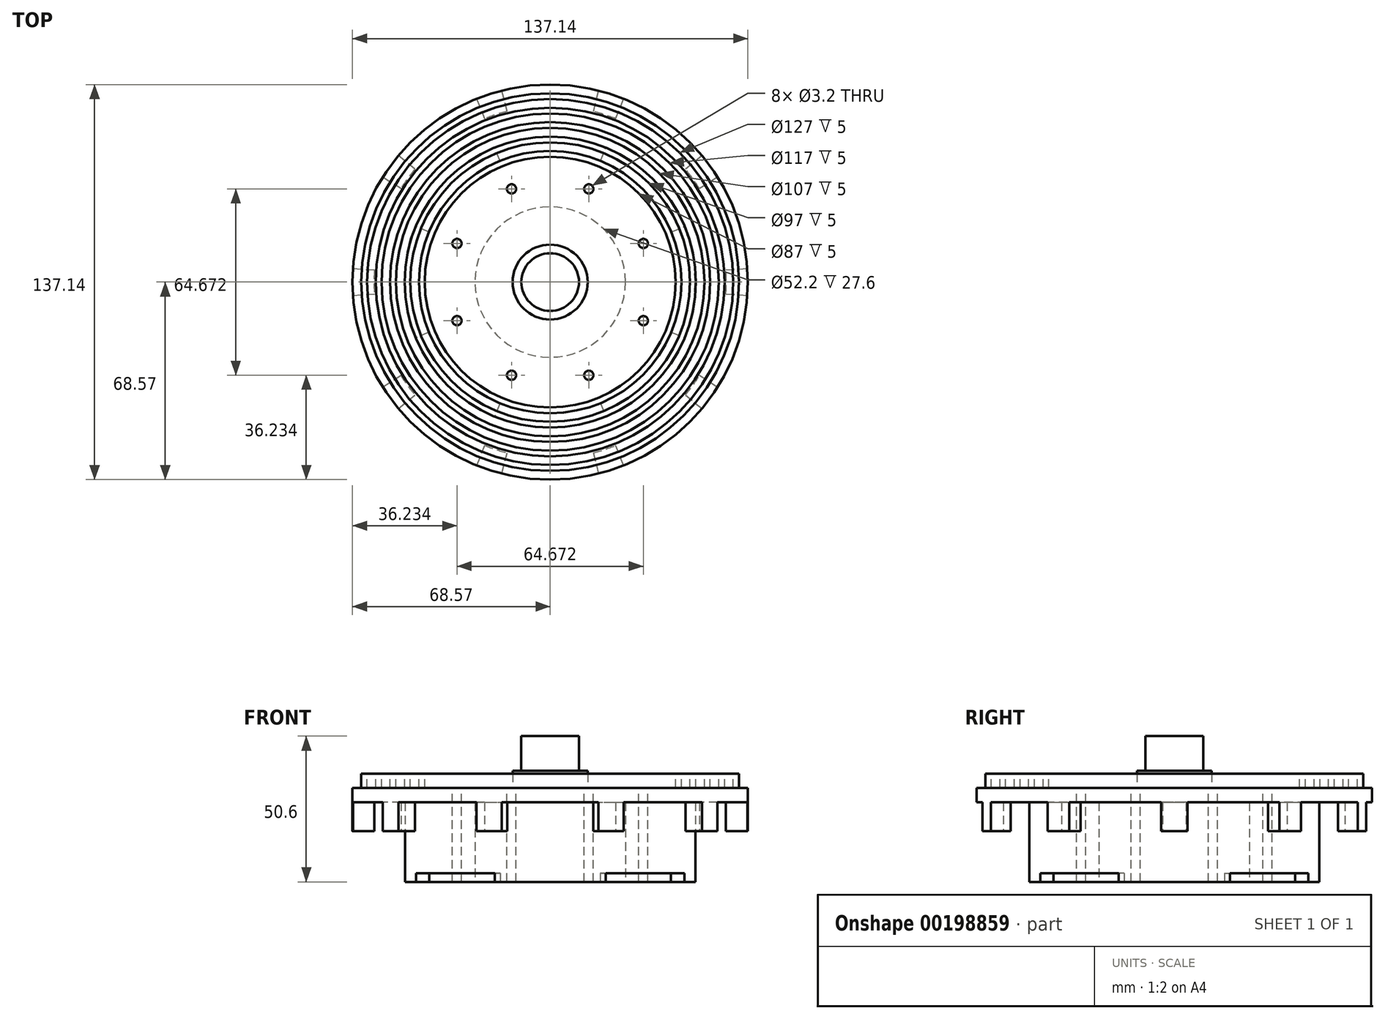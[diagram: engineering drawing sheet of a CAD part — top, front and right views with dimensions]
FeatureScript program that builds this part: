
annotation { "Feature Type Name" : "Feature", "Feature Type Description" : "" }
export const myFeature = defineFeature(function(context is Context, id is Id, definition is map)
    precondition{}
    {
        {
            var Q0;
            Q0=qCreatedBy(makeId("Top.planeOp"),FACE);
            var sketch = newSketch(context, id + "F0", { "sketchPlane" : qUnion([Q0])});
            skCircle(sketch, "E0", {"center": v(0, 0) * mm, "radius": 50.15 * mm, "construction": true});
            skCircle(sketch, "E1", {"center": v(0, 0) * mm, "radius": 68.57 * mm});
            skCircle(sketch, "E2", {"center": v(0, 0) * mm, "radius": 61.01 * mm, "construction": true});
            skSolve(sketch);
        }
        {
            var Q0;
            Q0=qSketchRegion(id+"F0",true);
            extrude(context, id + "F1", {"entities" : qUnion([Q0]), "depth" : 27.6 * mm});
        }
        {
            var Q0;
            Q0=makeQuery(id+"F1.opExtrude","CAP_FACE",FACE,{"disambiguationData":[OSD([sQuery(id+"F0.wireOp",EDGE,"E1")])],"isStart":true});
            var sketch = newSketch(context, id + "F2", { "sketchPlane" : qUnion([Q0])});
            skLineSegment(sketch, "E3", {"start": v(0, 0) * mm, "end": v(-16.76, -66.49) * mm, "construction": true});
            skLineSegment(sketch, "E4", {"start": v(0, 0) * mm, "end": v(20.02, -79.4) * mm, "construction": true});
            skLineSegment(sketch, "E5", {"start": v(-14.91, -59.15) * mm, "end": v(14.91, -59.15) * mm});
            skLineSegment(sketch, "E6", {"start": v(-14.91, -59.15) * mm, "end": v(-18.58, -73.7) * mm});
            skLineSegment(sketch, "E7", {"start": v(-18.58, -73.7) * mm, "end": v(18.58, -73.7) * mm});
            skLineSegment(sketch, "E8", {"start": v(18.58, -73.7) * mm, "end": v(14.91, -59.15) * mm});
            skSolve(sketch);
        }
        {
            var Q0;
            Q0=qSketchRegion(id+"F2",true);
            extrude(context, id + "F3", {"entities" : qUnion([Q0]), "endBound" : BoundingType.SYMMETRIC, "depth" : 75 * mm});
        }
        {
            var Q0;
            Q0=makeQuery(id+"F3.opExtrude","SWEPT_BODY",BODY,{"disambiguationData":[OSD([sQuery(id+"F2.wireOp",EDGE,"E5"),sQuery(id+"F2.wireOp",EDGE,"E6"),sQuery(id+"F2.wireOp",EDGE,"E7"),sQuery(id+"F2.wireOp",EDGE,"E8")])]});
            var Q1;
            Q1=makeQuery(id+"F1.opExtrude","SWEPT_FACE",FACE,{"disambiguationData":[OSD([sQuery(id+"F0.wireOp",EDGE,"E1")])]});
            circularPattern(context, id + "F4", {"entities" : qUnion([Q0]), "axis" : qUnion([Q1]), "angle" : 36 * degree, "instanceCount" : 10});
        }
        {
            var Q0;
            Q0=makeQuery(id+"F4.opPattern","COPY",BODY,{"derivedFrom":makeQuery(id+"F3.opExtrude","SWEPT_BODY",BODY,{"disambiguationData":[OSD([sQuery(id+"F2.wireOp",EDGE,"E5"),sQuery(id+"F2.wireOp",EDGE,"E6"),sQuery(id+"F2.wireOp",EDGE,"E7"),sQuery(id+"F2.wireOp",EDGE,"E8")])]}),"instanceName":"7"});
            var Q1;
            Q1=makeQuery(id+"F4.opPattern","COPY",BODY,{"derivedFrom":makeQuery(id+"F3.opExtrude","SWEPT_BODY",BODY,{"disambiguationData":[OSD([sQuery(id+"F2.wireOp",EDGE,"E5"),sQuery(id+"F2.wireOp",EDGE,"E6"),sQuery(id+"F2.wireOp",EDGE,"E7"),sQuery(id+"F2.wireOp",EDGE,"E8")])]}),"instanceName":"8"});
            var Q2;
            Q2=makeQuery(id+"F4.opPattern","COPY",BODY,{"derivedFrom":makeQuery(id+"F3.opExtrude","SWEPT_BODY",BODY,{"disambiguationData":[OSD([sQuery(id+"F2.wireOp",EDGE,"E5"),sQuery(id+"F2.wireOp",EDGE,"E6"),sQuery(id+"F2.wireOp",EDGE,"E7"),sQuery(id+"F2.wireOp",EDGE,"E8")])]}),"instanceName":"9"});
            var Q3;
            Q3=makeQuery(id+"F3.opExtrude","SWEPT_BODY",BODY,{"disambiguationData":[OSD([sQuery(id+"F2.wireOp",EDGE,"E5"),sQuery(id+"F2.wireOp",EDGE,"E6"),sQuery(id+"F2.wireOp",EDGE,"E7"),sQuery(id+"F2.wireOp",EDGE,"E8")])]});
            var Q4;
            Q4=makeQuery(id+"F4.opPattern","COPY",BODY,{"derivedFrom":makeQuery(id+"F3.opExtrude","SWEPT_BODY",BODY,{"disambiguationData":[OSD([sQuery(id+"F2.wireOp",EDGE,"E5"),sQuery(id+"F2.wireOp",EDGE,"E6"),sQuery(id+"F2.wireOp",EDGE,"E7"),sQuery(id+"F2.wireOp",EDGE,"E8")])]}),"instanceName":"1"});
            var Q5;
            Q5=makeQuery(id+"F4.opPattern","COPY",BODY,{"derivedFrom":makeQuery(id+"F3.opExtrude","SWEPT_BODY",BODY,{"disambiguationData":[OSD([sQuery(id+"F2.wireOp",EDGE,"E5"),sQuery(id+"F2.wireOp",EDGE,"E6"),sQuery(id+"F2.wireOp",EDGE,"E7"),sQuery(id+"F2.wireOp",EDGE,"E8")])]}),"instanceName":"2"});
            var Q6;
            Q6=makeQuery(id+"F4.opPattern","COPY",BODY,{"derivedFrom":makeQuery(id+"F3.opExtrude","SWEPT_BODY",BODY,{"disambiguationData":[OSD([sQuery(id+"F2.wireOp",EDGE,"E5"),sQuery(id+"F2.wireOp",EDGE,"E6"),sQuery(id+"F2.wireOp",EDGE,"E7"),sQuery(id+"F2.wireOp",EDGE,"E8")])]}),"instanceName":"3"});
            var Q7;
            Q7=makeQuery(id+"F4.opPattern","COPY",BODY,{"derivedFrom":makeQuery(id+"F3.opExtrude","SWEPT_BODY",BODY,{"disambiguationData":[OSD([sQuery(id+"F2.wireOp",EDGE,"E5"),sQuery(id+"F2.wireOp",EDGE,"E6"),sQuery(id+"F2.wireOp",EDGE,"E7"),sQuery(id+"F2.wireOp",EDGE,"E8")])]}),"instanceName":"4"});
            var Q8;
            Q8=makeQuery(id+"F4.opPattern","COPY",BODY,{"derivedFrom":makeQuery(id+"F3.opExtrude","SWEPT_BODY",BODY,{"disambiguationData":[OSD([sQuery(id+"F2.wireOp",EDGE,"E5"),sQuery(id+"F2.wireOp",EDGE,"E6"),sQuery(id+"F2.wireOp",EDGE,"E7"),sQuery(id+"F2.wireOp",EDGE,"E8")])]}),"instanceName":"5"});
            var Q9;
            Q9=makeQuery(id+"F4.opPattern","COPY",BODY,{"derivedFrom":makeQuery(id+"F3.opExtrude","SWEPT_BODY",BODY,{"disambiguationData":[OSD([sQuery(id+"F2.wireOp",EDGE,"E5"),sQuery(id+"F2.wireOp",EDGE,"E6"),sQuery(id+"F2.wireOp",EDGE,"E7"),sQuery(id+"F2.wireOp",EDGE,"E8")])]}),"instanceName":"6"});
            var Q10;
            Q10=makeQuery(id+"F1.opExtrude","SWEPT_BODY",BODY,{"disambiguationData":[OSD([sQuery(id+"F0.wireOp",EDGE,"E1")])]});
            booleanBodies(context, id + "F5", {"operationType" : BooleanOperationType.SUBTRACTION, "tools" : qUnion([Q0, Q1, Q2, Q3, Q4, Q5, Q6, Q7, Q8, Q9]), "targets" : qUnion([Q10])});
        }
        {
            var Q0;
            Q0=makeQuery(id+"F1.opExtrude","CAP_FACE",FACE,{"disambiguationData":[OSD([sQuery(id+"F0.wireOp",EDGE,"E1")])],"isStart":false});
            var sketch = newSketch(context, id + "F6", { "sketchPlane" : qUnion([Q0])});
            skCircle(sketch, "E9", {"center": v(0, 0) * mm, "radius": 68.57 * mm});
            skSolve(sketch);
        }
        {
            var Q0;
            Q0=qSketchRegion(id+"F6",true);
            extrude(context, id + "F7", {"entities" : qUnion([Q0]), "operationType" : NewBodyOperationType.ADD, "depth" : 10 * mm});
        }
        {
            var Q0;
            Q0=makeQuery(id+"F1.opExtrude","CAP_FACE",FACE,{"disambiguationData":[OSD([sQuery(id+"F0.wireOp",EDGE,"E1")])],"isStart":true});
            var sketch = newSketch(context, id + "F8", { "sketchPlane" : qUnion([Q0])});
            skCircle(sketch, "E10", {"center": v(0, 0) * mm, "radius": 50.35 * mm});
            skCircle(sketch, "E11", {"center": v(0, 0) * mm, "radius": 61.1 * mm});
            skSolve(sketch);
        }
        {
            var Q0;
            Q0=qSketchRegion(id+"F8",true);
            extrude(context, id + "F9", {"entities" : qUnion([Q0]), "operationType" : NewBodyOperationType.REMOVE, "oppositeDirection" : true, "depth" : 27.6 * mm});
        }
        {
            var Q0;
            Q0=qCreatedBy(makeId("Front.planeOp"),FACE);
            var sketch = newSketch(context, id + "F10", { "sketchPlane" : qUnion([Q0])});
            skLineSegment(sketch, "E12", {"start": v(0, 42.6) * mm, "end": v(-100, 42.6) * mm});
            skLineSegment(sketch, "E13", {"start": v(-100, 42.6) * mm, "end": v(-100, 32.6) * mm});
            skLineSegment(sketch, "E14", {"start": v(-100, 32.6) * mm, "end": v(-65.5, 32.6) * mm});
            skLineSegment(sketch, "E15", {"start": v(-65.5, 32.6) * mm, "end": v(-65.5, 39.6) * mm});
            skLineSegment(sketch, "E16", {"start": v(-65.5, 39.6) * mm, "end": v(-63.5, 39.6) * mm});
            skLineSegment(sketch, "E17", {"start": v(-63.5, 39.6) * mm, "end": v(-63.5, 32.6) * mm});
            skLineSegment(sketch, "E18", {"start": v(-63.5, 32.6) * mm, "end": v(-60.5, 32.6) * mm});
            skLineSegment(sketch, "E19", {"start": v(-60.5, 32.6) * mm, "end": v(-60.5, 39.6) * mm});
            skLineSegment(sketch, "E20", {"start": v(-60.5, 39.6) * mm, "end": v(-58.5, 39.6) * mm});
            skLineSegment(sketch, "E21", {"start": v(-58.5, 39.6) * mm, "end": v(-58.5, 32.6) * mm});
            skLineSegment(sketch, "E22", {"start": v(-58.5, 32.6) * mm, "end": v(-55.5, 32.6) * mm});
            skLineSegment(sketch, "E23", {"start": v(-55.5, 32.6) * mm, "end": v(-55.5, 39.6) * mm});
            skLineSegment(sketch, "E24", {"start": v(-55.5, 39.6) * mm, "end": v(-53.5, 39.6) * mm});
            skLineSegment(sketch, "E25", {"start": v(-53.5, 39.6) * mm, "end": v(-53.5, 32.6) * mm});
            skLineSegment(sketch, "E26", {"start": v(-53.5, 32.6) * mm, "end": v(-50.5, 32.6) * mm});
            skLineSegment(sketch, "E27", {"start": v(-50.5, 32.6) * mm, "end": v(-50.5, 39.6) * mm});
            skLineSegment(sketch, "E28", {"start": v(-50.5, 39.6) * mm, "end": v(-48.5, 39.6) * mm});
            skLineSegment(sketch, "E29", {"start": v(-48.5, 39.6) * mm, "end": v(-48.5, 32.6) * mm});
            skLineSegment(sketch, "E30", {"start": v(-48.5, 32.6) * mm, "end": v(-45.5, 32.6) * mm});
            skLineSegment(sketch, "E31", {"start": v(-45.5, 32.6) * mm, "end": v(-45.5, 39.6) * mm});
            skLineSegment(sketch, "E32", {"start": v(-45.5, 39.6) * mm, "end": v(-43.5, 39.6) * mm});
            skLineSegment(sketch, "E33", {"start": v(-43.5, 39.6) * mm, "end": v(-43.5, 32.6) * mm});
            skLineSegment(sketch, "E34", {"start": v(-43.5, 32.6) * mm, "end": v(0, 32.6) * mm});
            skLineSegment(sketch, "E35", {"start": v(0, 32.6) * mm, "end": v(0, 42.6) * mm});
            skSolve(sketch);
        }
        {
            var Q0;
            Q0=qSketchRegion(id+"F10",true);
            var Q1;
            Q1=sQuery(id+"F10.wireOp",EDGE,"E35");
            revolve(context, id + "F11", {"operationType" : NewBodyOperationType.REMOVE, "entities" : qUnion([Q0]), "axis" : qUnion([Q1]), "revolveType" : RevolveType.FULL, "oppositeDirection" : true});
        }
        {
            var Q0;
            Q0=makeQuery(id+"F11.boolean.opBoolean","COPY",FACE,{"derivedFrom":makeQuery(id+"F11.opRevolve","SWEPT_FACE",FACE,{"disambiguationData":[OSD([sQuery(id+"F10.wireOp",EDGE,"E34")])]})});
            var sketch = newSketch(context, id + "F12", { "sketchPlane" : qUnion([Q0])});
            skCircle(sketch, "E36", {"center": v(0, 0) * mm, "radius": 13 * mm});
            skSolve(sketch);
        }
        {
            var Q0;
            Q0=qSketchRegion(id+"F12",true);
            extrude(context, id + "F13", {"entities" : qUnion([Q0]), "operationType" : NewBodyOperationType.ADD, "depth" : 6 * mm});
        }
        {
            var Q0;
            Q0=makeQuery(id+"F13.opExtrude","CAP_FACE",FACE,{"disambiguationData":[OSD([sQuery(id+"F12.wireOp",EDGE,"E36")])],"isStart":false});
            var sketch = newSketch(context, id + "F14", { "sketchPlane" : qUnion([Q0])});
            skCircle(sketch, "E37", {"center": v(0, 0) * mm, "radius": 10 * mm});
            skSolve(sketch);
        }
        {
            var Q0;
            Q0=qSketchRegion(id+"F14",true);
            extrude(context, id + "F15", {"entities" : qUnion([Q0]), "operationType" : NewBodyOperationType.ADD, "depth" : 12 * mm});
        }
        {
            var Q0;
            Q0=makeQuery(id+"F9.boolean.opBoolean","SPLIT",FACE,{"disambiguationData":[TD([makeQuery(id+"F9.opExtrude","SWEPT_FACE",FACE,{"disambiguationData":[OSD([sQuery(id+"F8.wireOp",EDGE,"E10")])]})])],"derivedFrom":makeQuery(id+"F1.opExtrude","CAP_FACE",FACE,{"disambiguationData":[OSD([sQuery(id+"F0.wireOp",EDGE,"E1")])],"isStart":true})});
            var sketch = newSketch(context, id + "F16", { "sketchPlane" : qUnion([Q0])});
            skCircle(sketch, "E38", {"center": v(0, 0) * mm, "radius": 55 * mm});
            skCircle(sketch, "E39", {"center": v(0, 0) * mm, "radius": 90 * mm});
            skSolve(sketch);
        }
        {
            var Q0;
            Q0=qSketchRegion(id+"F16",true);
            extrude(context, id + "F17", {"entities" : qUnion([Q0]), "operationType" : NewBodyOperationType.REMOVE, "oppositeDirection" : true, "depth" : 17.6 * mm});
        }
        {
            var Q0;
            Q0=makeQuery(id+"F9.boolean.opBoolean","SPLIT",FACE,{"disambiguationData":[TD([makeQuery(id+"F9.opExtrude","SWEPT_FACE",FACE,{"disambiguationData":[OSD([sQuery(id+"F8.wireOp",EDGE,"E10")])]})])],"derivedFrom":makeQuery(id+"F1.opExtrude","CAP_FACE",FACE,{"disambiguationData":[OSD([sQuery(id+"F0.wireOp",EDGE,"E1")])],"isStart":true})});
            var sketch = newSketch(context, id + "F18", { "sketchPlane" : qUnion([Q0])});
            skCircle(sketch, "E40", {"center": v(0, 0) * mm, "radius": 26.1 * mm});
            skSolve(sketch);
        }
        {
            var Q0;
            Q0=qSketchRegion(id+"F18",true);
            extrude(context, id + "F19", {"entities" : qUnion([Q0]), "operationType" : NewBodyOperationType.REMOVE, "oppositeDirection" : true, "depth" : 27.6 * mm});
        }
        {
            var Q0;
            Q0=makeQuery(id+"F11.boolean.opBoolean","COPY",FACE,{"derivedFrom":makeQuery(id+"F11.opRevolve","SWEPT_FACE",FACE,{"disambiguationData":[OSD([sQuery(id+"F10.wireOp",EDGE,"E34")])]})});
            var sketch = newSketch(context, id + "F20", { "sketchPlane" : qUnion([Q0])});
            skLineSegment(sketch, "E41", {"start": v(0, 0) * mm, "end": v(-16.96, -40.95) * mm, "construction": true});
            skPoint(sketch, "E42", {"position": v(-13.4, -32.34) * mm});
            skPoint(sketch, "E43.1.0", {"position": v(13.4, -32.34) * mm});
            skPoint(sketch, "E43.2.0", {"position": v(32.34, -13.4) * mm});
            skPoint(sketch, "E43.3.0", {"position": v(32.34, 13.4) * mm});
            skPoint(sketch, "E43.4.0", {"position": v(13.4, 32.34) * mm});
            skPoint(sketch, "E43.5.0", {"position": v(-13.4, 32.34) * mm});
            skPoint(sketch, "E43.6.0", {"position": v(-32.34, 13.4) * mm});
            skPoint(sketch, "E43.7.0", {"position": v(-32.34, -13.4) * mm});
            skPoint(sketch, "E43.center", {"position": v(0, 0) * mm});
            skSolve(sketch);
        }
        {
            var Q0;
            Q0=sQuery(id+"F20.wireOp",VERTEX,"E42");
            var Q1;
            Q1=sQuery(id+"F20.wireOp",VERTEX,"E43.1.0");
            var Q2;
            Q2=sQuery(id+"F20.wireOp",VERTEX,"E43.2.0");
            var Q3;
            Q3=sQuery(id+"F20.wireOp",VERTEX,"E43.3.0");
            var Q4;
            Q4=sQuery(id+"F20.wireOp",VERTEX,"E43.4.0");
            var Q5;
            Q5=sQuery(id+"F20.wireOp",VERTEX,"E43.5.0");
            var Q6;
            Q6=sQuery(id+"F20.wireOp",VERTEX,"E43.6.0");
            var Q7;
            Q7=sQuery(id+"F20.wireOp",VERTEX,"E43.7.0");
            var Q8;
            Q8=makeQuery(id+"F1.opExtrude","SWEPT_BODY",BODY,{"disambiguationData":[OSD([sQuery(id+"F0.wireOp",EDGE,"E1")])]});
            hole(context, id + "F21", {"style" : HoleStyle.SIMPLE, "endStyle" : HoleEndStyle.THROUGH, "standardTappedOrClearance" : lookupTablePath({ "standard" : "ISO", "engagement" : "75%", "pitch" : "0.75 mm", "size" : "M4", "type" : "Tapped" }), "standardBlindInLast" : lookupTablePath({ "standard" : "ISO", "engagement" : "75%", "pitch" : "0.75 mm", "size" : "M4", "type" : "Tapped" }), "holeDiameter" : 3.2 * mm, "locations" : qUnion([Q0, Q1, Q2, Q3, Q4, Q5, Q6, Q7]), "scope" : qUnion([Q8]), "isTappedThrough" : true, "showTappedDepth" : true});
        }
        {
            var Q0;
            Q0=makeQuery(id+"F9.boolean.opBoolean","SPLIT",FACE,{"disambiguationData":[TD([makeQuery(id+"F9.opExtrude","SWEPT_FACE",FACE,{"disambiguationData":[OSD([sQuery(id+"F8.wireOp",EDGE,"E10")])]})])],"derivedFrom":makeQuery(id+"F1.opExtrude","CAP_FACE",FACE,{"disambiguationData":[OSD([sQuery(id+"F0.wireOp",EDGE,"E1")])],"isStart":true})});
            var sketch = newSketch(context, id + "F22", { "sketchPlane" : qUnion([Q0])});
            skLineSegment(sketch, "E44", {"start": v(0, 0) * mm, "end": v(37.55, 37.55) * mm, "construction": true});
            skLineSegment(sketch, "E45", {"start": v(0, 0) * mm, "end": v(56.18, 23.27) * mm, "construction": true});
            skLineSegment(sketch, "E46", {"start": v(41.9, 17.35) * mm, "end": v(46.52, 19.27) * mm});
            skArc(sketch, "E47", {"start": v(41.9, 17.35) * mm, "mid": v(37.7, 25.2) * mm, "end": v(32.07, 32.07) * mm});
            skArc(sketch, "E48", {"start": v(46.52, 19.27) * mm, "mid": v(41.86, 27.97) * mm, "end": v(35.6, 35.6) * mm});
            skArc(sketch, "E49.MirrorCS", {"start": v(19.27, 46.52) * mm, "mid": v(27.97, 41.86) * mm, "end": v(35.6, 35.6) * mm});
            skLineSegment(sketch, "E50.MirrorCS", {"start": v(17.35, 41.9) * mm, "end": v(19.27, 46.52) * mm});
            skArc(sketch, "E51.MirrorCS", {"start": v(17.35, 41.9) * mm, "mid": v(25.2, 37.7) * mm, "end": v(32.07, 32.07) * mm});
            skLineSegment(sketch, "E52.MirrorCS", {"start": v(-17.35, 41.9) * mm, "end": v(-19.27, 46.52) * mm});
            skArc(sketch, "E53.MirrorCS", {"start": v(-19.27, 46.52) * mm, "mid": v(-27.97, 41.86) * mm, "end": v(-35.6, 35.6) * mm});
            skArc(sketch, "E54.MirrorCS", {"start": v(-46.52, 19.27) * mm, "mid": v(-41.86, 27.97) * mm, "end": v(-35.6, 35.6) * mm});
            skLineSegment(sketch, "E55.MirrorCS", {"start": v(-41.9, 17.35) * mm, "end": v(-46.52, 19.27) * mm});
            skArc(sketch, "E56.MirrorCS", {"start": v(-41.9, 17.35) * mm, "mid": v(-37.7, 25.2) * mm, "end": v(-32.07, 32.07) * mm});
            skArc(sketch, "E57.MirrorCS", {"start": v(-17.35, 41.9) * mm, "mid": v(-25.2, 37.7) * mm, "end": v(-32.07, 32.07) * mm});
            skLineSegment(sketch, "E58.MirrorCS", {"start": v(41.9, -17.35) * mm, "end": v(46.52, -19.27) * mm});
            skArc(sketch, "E59.MirrorCS", {"start": v(41.9, -17.35) * mm, "mid": v(37.7, -25.2) * mm, "end": v(32.07, -32.07) * mm});
            skArc(sketch, "E60.MirrorCS", {"start": v(17.35, -41.9) * mm, "mid": v(25.2, -37.7) * mm, "end": v(32.07, -32.07) * mm});
            skLineSegment(sketch, "E61.MirrorCS", {"start": v(17.35, -41.9) * mm, "end": v(19.27, -46.52) * mm});
            skArc(sketch, "E62.MirrorCS", {"start": v(19.27, -46.52) * mm, "mid": v(27.97, -41.86) * mm, "end": v(35.6, -35.6) * mm});
            skArc(sketch, "E63.MirrorCS", {"start": v(46.52, -19.27) * mm, "mid": v(41.86, -27.97) * mm, "end": v(35.6, -35.6) * mm});
            skArc(sketch, "E64.MirrorCS", {"start": v(-17.35, -41.9) * mm, "mid": v(-25.2, -37.7) * mm, "end": v(-32.07, -32.07) * mm});
            skArc(sketch, "E65.MirrorCS", {"start": v(-41.9, -17.35) * mm, "mid": v(-37.7, -25.2) * mm, "end": v(-32.07, -32.07) * mm});
            skLineSegment(sketch, "E66.MirrorCS", {"start": v(-41.9, -17.35) * mm, "end": v(-46.52, -19.27) * mm});
            skArc(sketch, "E67.MirrorCS", {"start": v(-46.52, -19.27) * mm, "mid": v(-41.86, -27.97) * mm, "end": v(-35.6, -35.6) * mm});
            skArc(sketch, "E68.MirrorCS", {"start": v(-19.27, -46.52) * mm, "mid": v(-27.97, -41.86) * mm, "end": v(-35.6, -35.6) * mm});
            skLineSegment(sketch, "E69.MirrorCS", {"start": v(-17.35, -41.9) * mm, "end": v(-19.27, -46.52) * mm});
            skSolve(sketch);
        }
        {
            var Q0;
            Q0=qSketchRegion(id+"F22",true);
            extrude(context, id + "F23", {"entities" : qUnion([Q0]), "operationType" : NewBodyOperationType.REMOVE, "oppositeDirection" : true, "depth" : 3 * mm});
        }
    });
